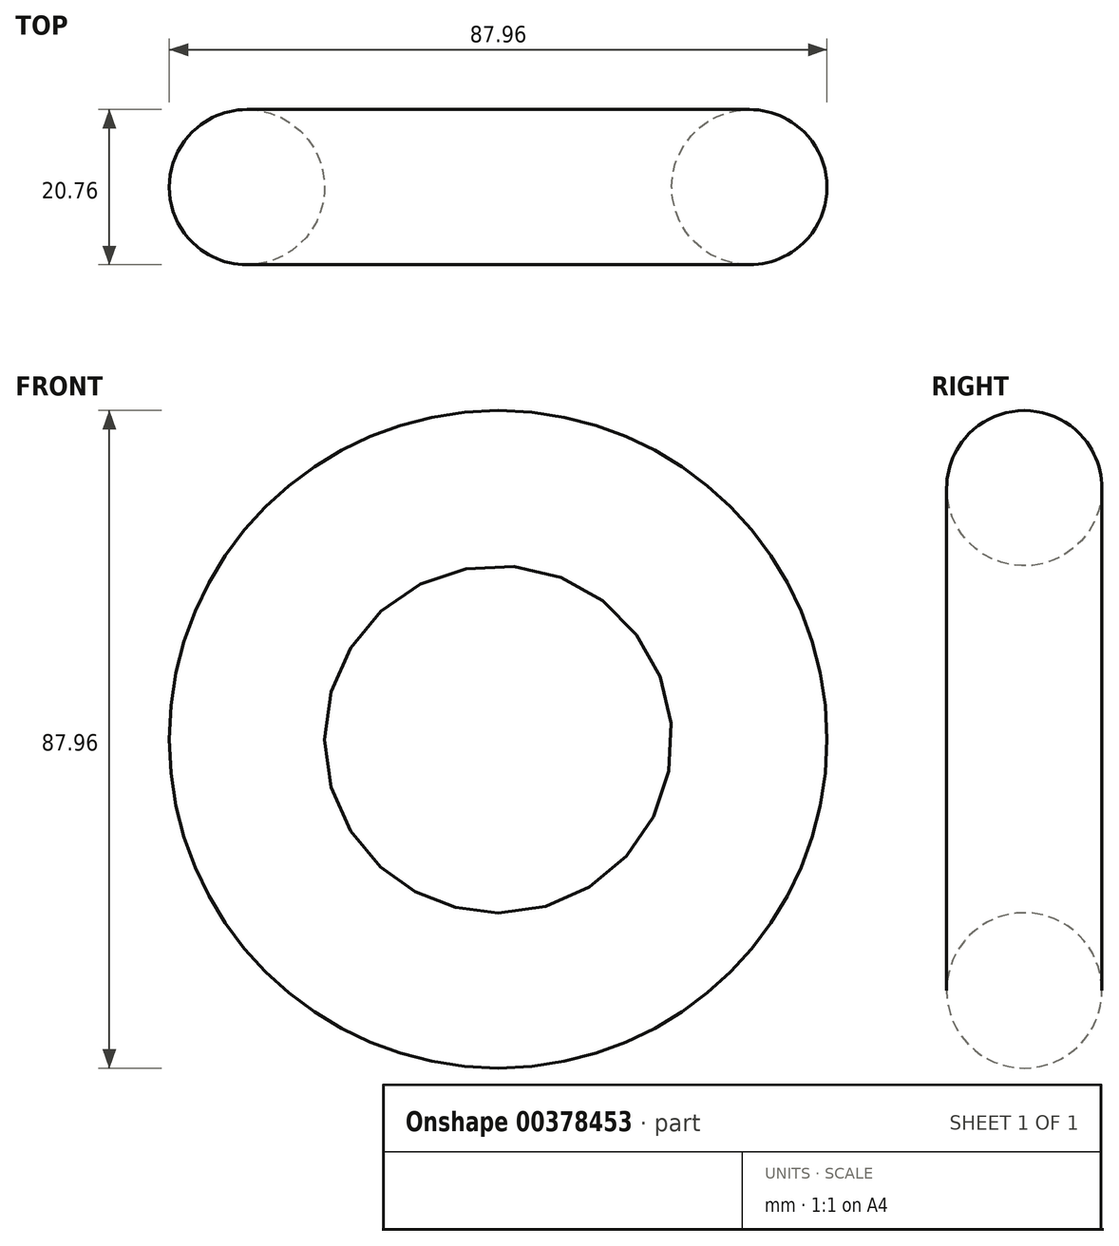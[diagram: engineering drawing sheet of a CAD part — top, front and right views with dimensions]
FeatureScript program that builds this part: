
annotation { "Feature Type Name" : "Feature", "Feature Type Description" : "" }
export const myFeature = defineFeature(function(context is Context, id is Id, definition is map)
    precondition{}
    {
        {
            var Q0;
            Q0=qCreatedBy(makeId("Top.planeOp"),FACE);
            var sketch = newSketch(context, id + "F0", { "sketchPlane" : qUnion([Q0])});
            skCircle(sketch, "E0", {"center": v(-33.6, 0) * mm, "radius": 10.38 * mm});
            skLineSegment(sketch, "E1", {"start": v(0, 0) * mm, "end": v(0, 44.42) * mm, "construction": true});
            skSolve(sketch);
        }
        {
            var Q0;
            Q0=makeQuery(id+"F0.imprint","IMPRINT",FACE,{"disambiguationData":[TD([[makeQuery(id+"F0.imprint","IMPRINT",EDGE,{"derivedFrom":sQuery(id+"F0.wireOp",EDGE,"E0")}),1.0]])]});
            var Q1;
            Q1=sQuery(id+"F0.wireOp",EDGE,"E1");
            revolve(context, id + "F1", {"entities" : qUnion([Q0]), "axis" : qUnion([Q1]), "revolveType" : RevolveType.FULL});
        }
    });
